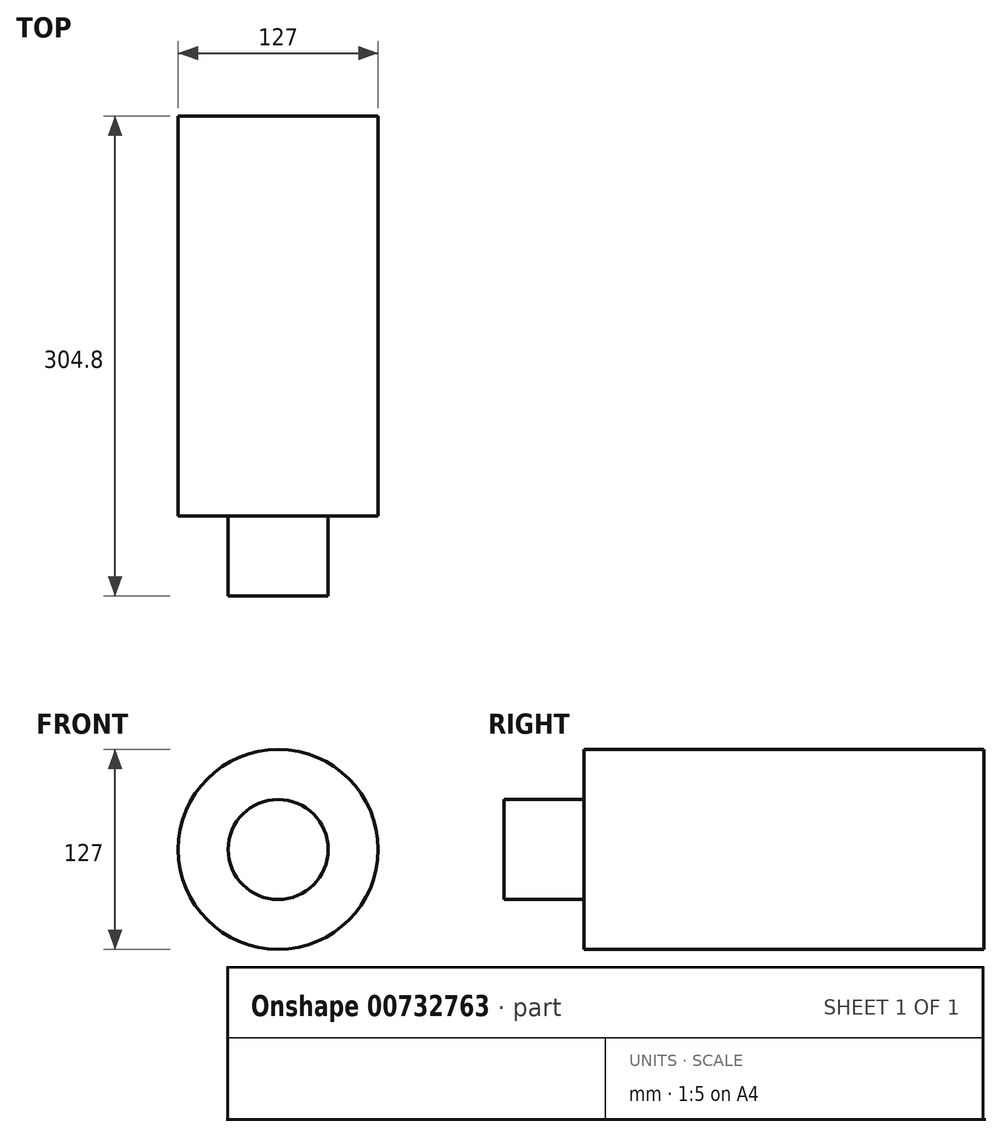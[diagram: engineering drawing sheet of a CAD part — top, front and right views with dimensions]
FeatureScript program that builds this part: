
annotation { "Feature Type Name" : "Feature", "Feature Type Description" : "" }
export const myFeature = defineFeature(function(context is Context, id is Id, definition is map)
    precondition{}
    {
        {
            var Q0;
            Q0=qCreatedBy(makeId("Front.planeOp"),FACE);
            var sketch = newSketch(context, id + "F0", { "sketchPlane" : qUnion([Q0])});
            skCircle(sketch, "E0", {"center": v(0, 0) * mm, "radius": 63.5 * mm});
            skSolve(sketch);
        }
        {
            var Q0;
            Q0=makeQuery(id+"F0.imprint","IMPRINT",FACE,{"disambiguationData":[TD([[makeQuery(id+"F0.imprint","IMPRINT",EDGE,{"derivedFrom":sQuery(id+"F0.wireOp",EDGE,"E0")}),1.0]])]});
            extrude(context, id + "F1", {"entities" : qUnion([Q0]), "depth" : 254 * mm, "offsetDistance" : 25.4 * mm});
        }
        {
            var Q0;
            Q0=makeQuery(id+"F1.opExtrude","CAP_FACE",FACE,{"disambiguationData":[OSD([sQuery(id+"F0.wireOp",EDGE,"E0")])],"isStart":false});
            var sketch = newSketch(context, id + "F2", { "sketchPlane" : qUnion([Q0])});
            skCircle(sketch, "E1", {"center": v(0, 0) * mm, "radius": 31.75 * mm});
            skSolve(sketch);
        }
        {
            var Q0;
            Q0=makeQuery(id+"F2.imprint","IMPRINT",FACE,{"disambiguationData":[TD([[makeQuery(id+"F2.imprint","IMPRINT",EDGE,{"derivedFrom":sQuery(id+"F2.wireOp",EDGE,"E1")}),1.0]])]});
            extrude(context, id + "F3", {"entities" : qUnion([Q0]), "operationType" : NewBodyOperationType.ADD, "depth" : 50.8 * mm, "offsetDistance" : 25.4 * mm});
        }
        {
            var Q0;
            Q0=qCreatedBy(makeId("Front.planeOp"),FACE);
            cPlane(context, id + "F4", {"entities" : qUnion([Q0]), "cplaneType" : CPlaneType.OFFSET, "offset" : 127 * mm, "width" : 152.4 * mm, "height" : 152.4 * mm});
        }
    });
